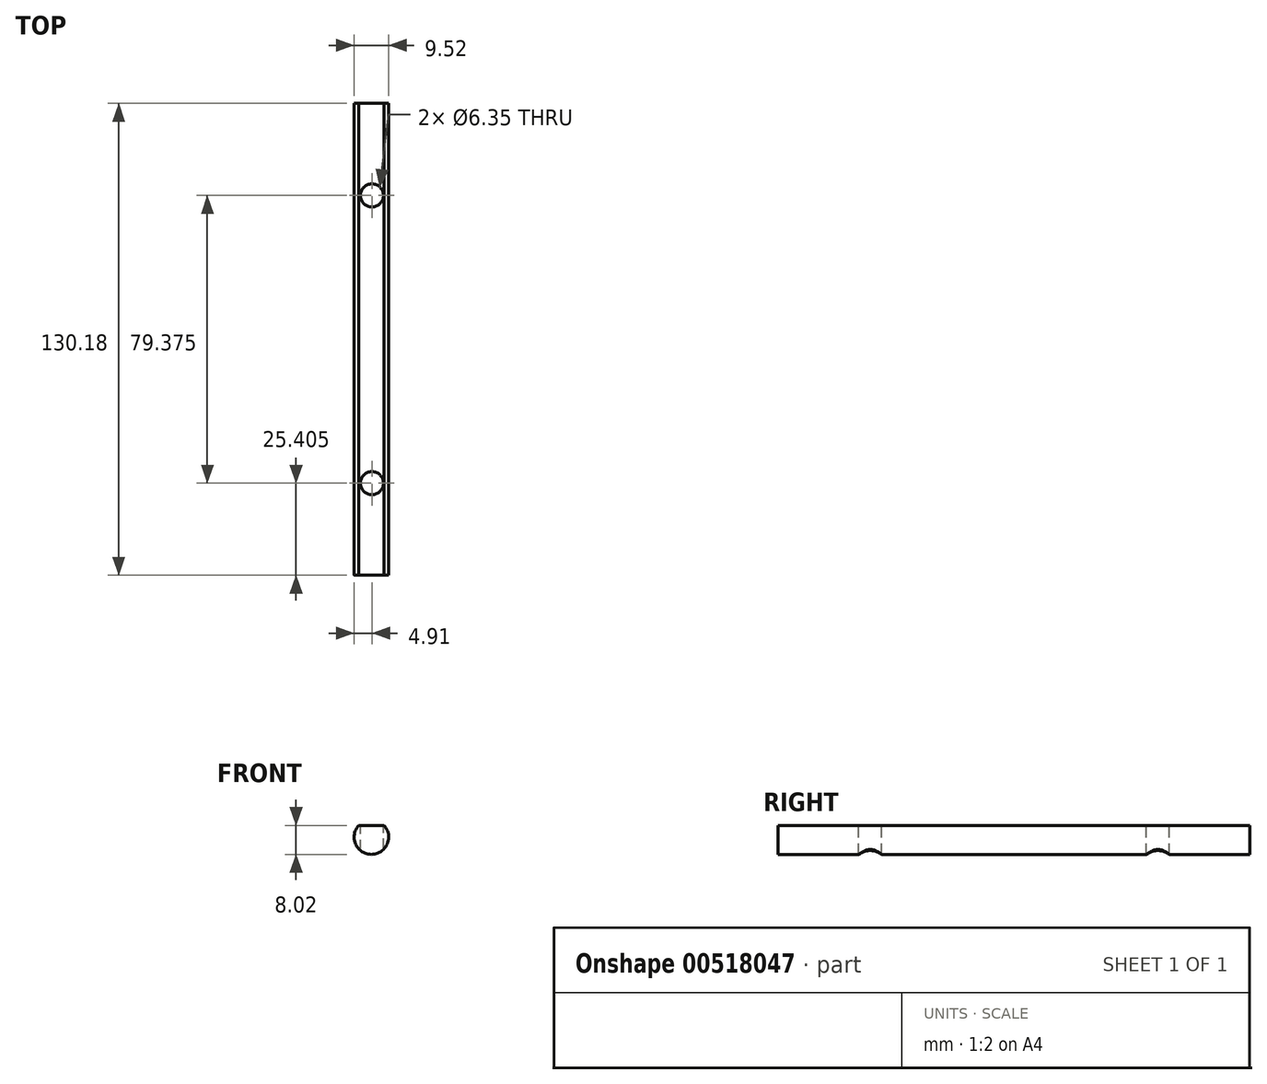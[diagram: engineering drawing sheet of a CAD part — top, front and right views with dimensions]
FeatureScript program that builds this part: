
annotation { "Feature Type Name" : "Feature", "Feature Type Description" : "" }
export const myFeature = defineFeature(function(context is Context, id is Id, definition is map)
    precondition{}
    {
        {
            var Q0;
            Q0=qCreatedBy(makeId("Front.planeOp"),FACE);
            var sketch = newSketch(context, id + "F0", { "sketchPlane" : qUnion([Q0])});
            skArc(sketch, "E0", {"start": v(-3.62, 5.36) * mm, "mid": v(-0.15, -2.66) * mm, "end": v(3.32, 5.36) * mm});
            skLineSegment(sketch, "E1", {"start": v(-3.62, 5.36) * mm, "end": v(3.32, 5.36) * mm});
            skSolve(sketch);
        }
        {
            var Q0;
            Q0=makeQuery(id+"F0.imprint","IMPRINT",FACE,{"disambiguationData":[TD([[makeQuery(id+"F0.imprint","IMPRINT",EDGE,{"derivedFrom":sQuery(id+"F0.wireOp",EDGE,"E0")}),1.0]])]});
            extrude(context, id + "F1", {"entities" : qUnion([Q0]), "depth" : 130.17 * mm});
        }
        {
            var Q0;
            Q0=makeQuery(id+"F1.opExtrude","SWEPT_FACE",FACE,{"disambiguationData":[OSD([sQuery(id+"F0.wireOp",EDGE,"E1")])]});
            var sketch = newSketch(context, id + "F2", { "sketchPlane" : qUnion([Q0])});
            skCircle(sketch, "E2", {"center": v(0, -25.4) * mm, "radius": 3.18 * mm});
            skCircle(sketch, "E3", {"center": v(0, -104.78) * mm, "radius": 3.18 * mm});
            skSolve(sketch);
        }
        {
            var Q0;
            Q0=sQuery(id+"F2.wireOp",VERTEX,"E2.center");
            var Q1;
            Q1=sQuery(id+"F2.wireOp",VERTEX,"E3.center");
            var Q2;
            Q2=makeQuery(id+"F1.opExtrude","SWEPT_BODY",BODY,{"disambiguationData":[OSD([sQuery(id+"F0.wireOp",EDGE,"E0"),sQuery(id+"F0.wireOp",EDGE,"E1")])]});
            hole(context, id + "F3", {"style" : HoleStyle.SIMPLE, "endStyle" : HoleEndStyle.THROUGH, "holeDiameter" : 6.35 * mm, "isTappedThrough" : true, "tappedDepth" : 12.7 * mm, "tapClearance" : 3, "locations" : qUnion([Q0, Q1]), "scope" : qUnion([Q2])});
        }
    });
